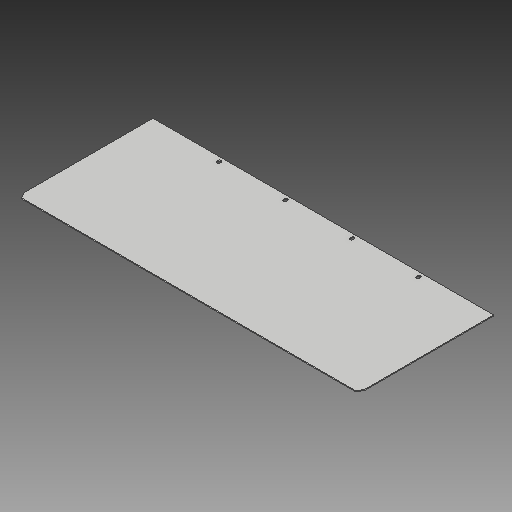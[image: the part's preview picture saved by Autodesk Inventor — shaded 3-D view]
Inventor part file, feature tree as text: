
AUTODESK INVENTOR PART (.ipt)
format: ipt  version: 2017 (Build 210142000, 142)  size: 92,672 bytes
history: native  units: in
note: dims shown in document units (in); Inventor stores cm internally (conversion verified against a paired STEP export)
features: chamfer x1
ambient origin geometry x8: Origin, YZ Plane, XZ Plane, XY Plane, X Axis, Y Axis, Z Axis, Center Point
bodies: Solid1 (feature_tree)
feature tree (1):
  chamfer  "Chamfer2"  [1 undecoded]
note: 1 required parameter value undecoded (feature->parameter linkage not recoverable at this tier; creation-order binding heuristic only, values carry confidence <= 0.55)
